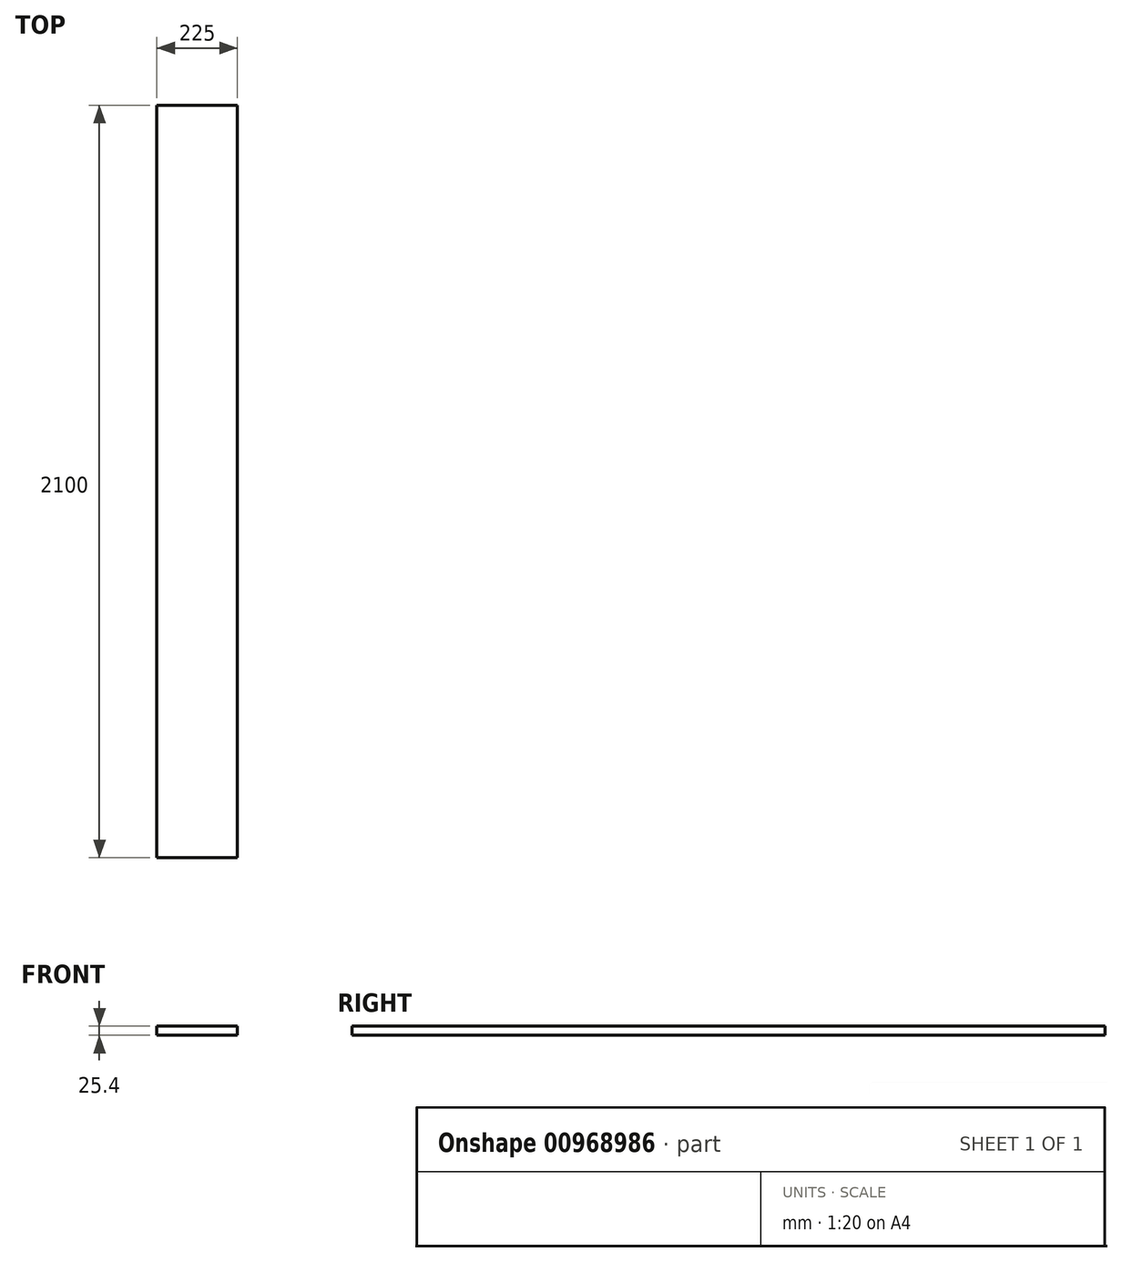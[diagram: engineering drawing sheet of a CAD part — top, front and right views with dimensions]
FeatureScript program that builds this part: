
annotation { "Feature Type Name" : "Feature", "Feature Type Description" : "" }
export const myFeature = defineFeature(function(context is Context, id is Id, definition is map)
    precondition{}
    {
        {
            var Q0;
            Q0=qCreatedBy(makeId("Top.planeOp"),FACE);
            var sketch = newSketch(context, id + "F0", { "sketchPlane" : qUnion([Q0])});
            skLineSegment(sketch, "E0.bottom", {"start": v(0, 0) * mm, "end": v(225, 0) * mm});
            skLineSegment(sketch, "E0.top", {"start": v(0, 2100) * mm, "end": v(225, 2100) * mm});
            skLineSegment(sketch, "E0.left", {"start": v(0, 0) * mm, "end": v(0, 2100) * mm});
            skLineSegment(sketch, "E0.right", {"start": v(225, 0) * mm, "end": v(225, 2100) * mm});
            skSolve(sketch);
        }
        {
            var Q0;
            Q0 = qSketchRegion(id + "F0", true);
            extrude(context, id + "F1", {"entities" : qUnion([Q0]), "depth" : 25.4 * mm, "offsetDistance" : 25.4 * mm});
        }
    });
